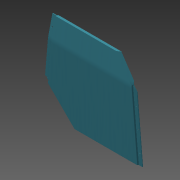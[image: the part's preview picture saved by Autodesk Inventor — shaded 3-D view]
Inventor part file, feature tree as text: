
AUTODESK INVENTOR PART (.ipt)
format: ipt  version: 2015 (Build 190159000, 159)  size: 1,085,952 bytes
history: native  units: mm
features: sketch x7, other x5, fillet x3, hole x2, extrude x2, loft x1, mirror x1, shell x1
ambient origin geometry x8: Origin, YZ Plane, XZ Plane, XY Plane, X Axis, Y Axis, Z Axis, Center Point
bodies: Body1 (feature_tree)
feature tree (22):
  sketch  "Szkic1"
  other  "Płaszczyzna konstrukcyjna2"
  loft  "Wyciągnięcie złożone2"
  other  "Płaszczyzna konstrukcyjna3"
  other  "Podział1"
  mirror  "Odbicie lustrzane1"
  shell  "Skorupa1"  Thickness=1.0mm
  fillet  "Zaokrąglenie1"  Radius=1.0mm
  fillet  "Zaokrąglenie3"  Radius=3.0mm
  hole  "Otwór3"  [1 undecoded]
  other  "Gięcie części2"
  extrude  "Wyciągnięcie proste6"  Depth=11.5mm
  extrude  "Wyciągnięcie proste7"  Depth=2.0mm
  fillet  "Zaokrąglenie5"  Radius=0.4mm
  hole  "Otwór4"  [1 undecoded]
  sketch  "Szkic9"
  other  "Bryła3"
  sketch  "Szkic11"
  sketch  "Szkic12"
  sketch  "Szkic14"
  sketch  "Szkic15"
  sketch  "Szkic16"
note: 2 required parameter values undecoded (feature->parameter linkage not recoverable at this tier; creation-order binding heuristic only, values carry confidence <= 0.55)
